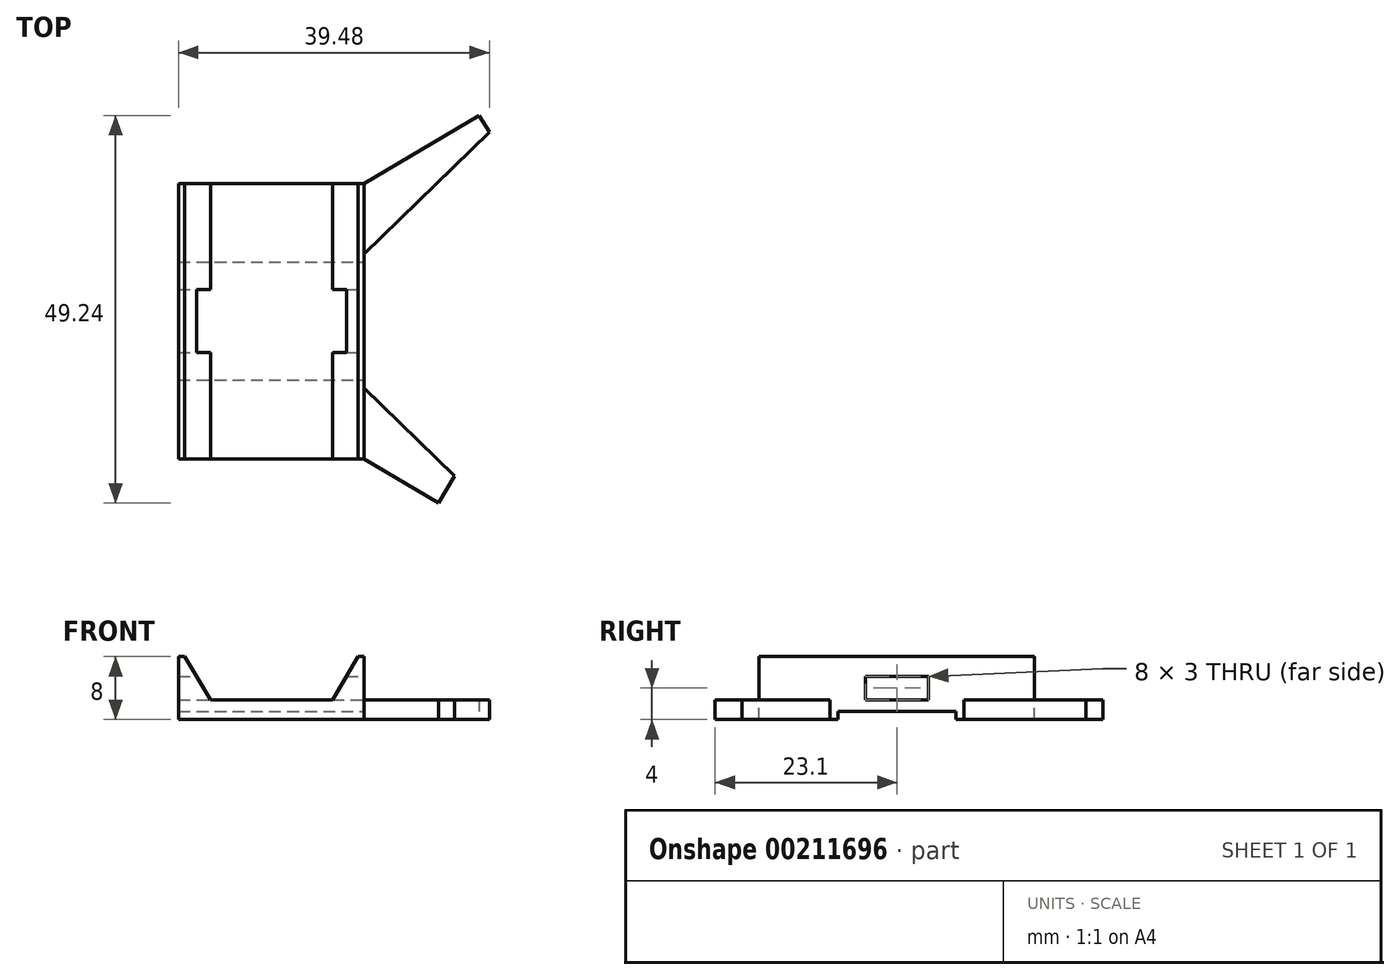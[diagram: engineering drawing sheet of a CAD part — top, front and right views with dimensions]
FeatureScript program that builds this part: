
annotation { "Feature Type Name" : "Feature", "Feature Type Description" : "" }
export const myFeature = defineFeature(function(context is Context, id is Id, definition is map)
    precondition{}
    {
        {
            var Q0;
            Q0=qCreatedBy(makeId("Front.planeOp"),FACE);
            var sketch = newSketch(context, id + "F0", { "sketchPlane" : qUnion([Q0])});
            skLineSegment(sketch, "E0", {"start": v(0, 0) * mm, "end": v(11.8, 0) * mm});
            skLineSegment(sketch, "E1", {"start": v(11.8, 0) * mm, "end": v(11.8, 8) * mm});
            skLineSegment(sketch, "E2", {"start": v(11.8, 8) * mm, "end": v(11, 8) * mm});
            skLineSegment(sketch, "E3", {"start": v(11, 8) * mm, "end": v(7.75, 2.5) * mm});
            skLineSegment(sketch, "E4", {"start": v(7.75, 2.5) * mm, "end": v(0, 2.5) * mm});
            skLineSegment(sketch, "E5.MirrorCS", {"start": v(0, 0) * mm, "end": v(-11.8, 0) * mm});
            skLineSegment(sketch, "E6.MirrorCS", {"start": v(-11.8, 8) * mm, "end": v(-11, 8) * mm});
            skLineSegment(sketch, "E7.MirrorCS", {"start": v(-7.75, 2.5) * mm, "end": v(0, 2.5) * mm});
            skLineSegment(sketch, "E8.MirrorCS", {"start": v(-11.8, 0) * mm, "end": v(-11.8, 8) * mm});
            skLineSegment(sketch, "E9.MirrorCS", {"start": v(-11, 8) * mm, "end": v(-7.75, 2.5) * mm});
            skSolve(sketch);
        }
        {
            var Q0;
            Q0=qSketchRegion(id+"F0",true);
            extrude(context, id + "F1", {"entities" : qUnion([Q0]), "endBound" : BoundingType.SYMMETRIC, "depth" : 35 * mm});
        }
        {
            var Q0;
            Q0=qCreatedBy(makeId("Right.planeOp"),FACE);
            var sketch = newSketch(context, id + "F2", { "sketchPlane" : qUnion([Q0])});
            skLineSegment(sketch, "E10.bottom", {"start": v(4, 2.5) * mm, "end": v(-4, 2.5) * mm});
            skLineSegment(sketch, "E10.top", {"start": v(4, 5.5) * mm, "end": v(-4, 5.5) * mm});
            skLineSegment(sketch, "E10.left", {"start": v(4, 2.5) * mm, "end": v(4, 5.5) * mm});
            skLineSegment(sketch, "E10.right", {"start": v(-4, 2.5) * mm, "end": v(-4, 5.5) * mm});
            skPoint(sketch, "E10.middle", {"position": v(0, 4) * mm});
            skLineSegment(sketch, "E11.bottom", {"start": v(-7.5, 0) * mm, "end": v(7.5, 0) * mm});
            skLineSegment(sketch, "E11.top", {"start": v(-7.5, 1) * mm, "end": v(7.5, 1) * mm});
            skLineSegment(sketch, "E11.left", {"start": v(-7.5, 0) * mm, "end": v(-7.5, 1) * mm});
            skLineSegment(sketch, "E11.right", {"start": v(7.5, 0) * mm, "end": v(7.5, 1) * mm});
            skSolve(sketch);
        }
        {
            var Q0;
            Q0=qSketchRegion(id+"F2",true);
            extrude(context, id + "F3", {"entities" : qUnion([Q0]), "operationType" : NewBodyOperationType.REMOVE, "endBound" : BoundingType.SYMMETRIC, "oppositeDirection" : true, "depth" : 100 * mm});
        }
        {
            var Q0;
            Q0=qCreatedBy(makeId("Top.planeOp"),FACE);
            var sketch = newSketch(context, id + "F4", { "sketchPlane" : qUnion([Q0])});
            skLineSegment(sketch, "E12", {"start": v(11.8, 17.5) * mm, "end": v(26.4, 26.14) * mm});
            skLineSegment(sketch, "E13", {"start": v(26.4, 26.14) * mm, "end": v(27.68, 24) * mm});
            skLineSegment(sketch, "E14", {"start": v(27.68, 24) * mm, "end": v(11.8, 8.5) * mm});
            skLineSegment(sketch, "E15", {"start": v(11.8, 8.5) * mm, "end": v(11.8, 17.5) * mm});
            skLineSegment(sketch, "E16", {"start": v(8.27, 0) * mm, "end": v(31.4, 0) * mm, "construction": true});
            skLineSegment(sketch, "E17.MirrorCS", {"start": v(11.8, -17.5) * mm, "end": v(21.26, -23.1) * mm});
            skLineSegment(sketch, "E18.MirrorCS", {"start": v(11.8, -8.5) * mm, "end": v(11.8, -17.5) * mm});
            skLineSegment(sketch, "E19.MirrorCS", {"start": v(23.27, -19.7) * mm, "end": v(11.8, -8.5) * mm});
            skLineSegment(sketch, "E20", {"start": v(21.26, -23.1) * mm, "end": v(23.27, -19.7) * mm});
            skPoint(sketch, "E21.MirrorCS.end.orphan", {"position": v(27.68, -24) * mm});
            skPoint(sketch, "E21.MirrorCS.start.orphan", {"position": v(26.4, -26.14) * mm});
            skSolve(sketch);
        }
        {
            var Q0;
            Q0=qSketchRegion(id+"F4",true);
            extrude(context, id + "F5", {"entities" : qUnion([Q0]), "operationType" : NewBodyOperationType.ADD, "depth" : 2.5 * mm});
        }
    });
